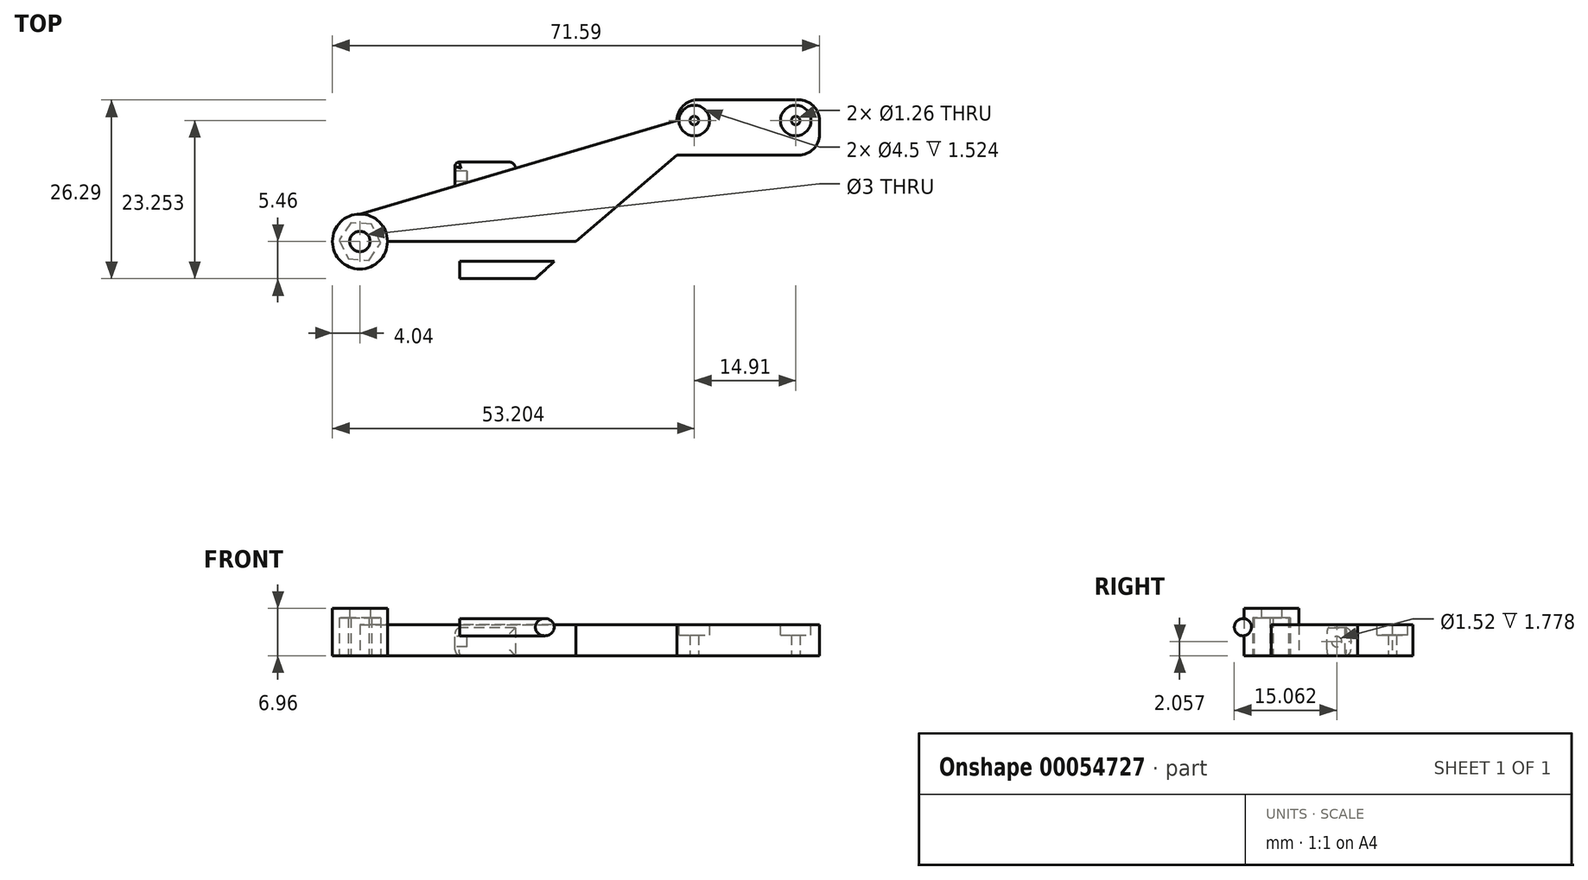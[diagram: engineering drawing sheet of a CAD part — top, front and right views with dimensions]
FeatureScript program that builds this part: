
annotation { "Feature Type Name" : "Feature", "Feature Type Description" : "" }
export const myFeature = defineFeature(function(context is Context, id is Id, definition is map)
    precondition{}
    {
        {
            var Q0;
            Q0=qCreatedBy(makeId("Top.planeOp"),FACE);
            var sketch = newSketch(context, id + "F0", { "sketchPlane" : qUnion([Q0])});
            skLineSegment(sketch, "E0", {"start": v(0, 0) * mm, "end": v(-31.75, 0) * mm});
            skLineSegment(sketch, "E1", {"start": v(-31.75, 0) * mm, "end": v(-46.62, 12.7) * mm});
            skLineSegment(sketch, "E2", {"start": v(-46.62, 12.7) * mm, "end": v(0, 0) * mm});
            skLineSegment(sketch, "E3", {"start": v(0, 0) * mm, "end": v(0, 4.04) * mm});
            skCircle(sketch, "E4", {"center": v(0, 0) * mm, "radius": 4.04 * mm});
            skLineSegment(sketch, "E5.bottom", {"start": v(-46.62, 12.7) * mm, "end": v(-64.5, 12.7) * mm});
            skLineSegment(sketch, "E5.top", {"start": v(-49.67, 20.83) * mm, "end": v(-64.5, 20.83) * mm});
            skLineSegment(sketch, "E5.left", {"start": v(-46.62, 12.7) * mm, "end": v(-46.62, 17.78) * mm});
            skLineSegment(sketch, "E5.right", {"start": v(-67.55, 15.75) * mm, "end": v(-67.55, 17.78) * mm});
            skCircle(sketch, "E6", {"center": v(-49.16, 17.8) * mm, "radius": 0.63 * mm});
            skCircle(sketch, "E7", {"center": v(-64.07, 17.8) * mm, "radius": 0.63 * mm});
            skPoint(sketch, "E8.visualSharp", {"position": v(-67.55, 20.83) * mm});
            skArc(sketch, "E8.filletArc", {"start": v(-64.5, 20.83) * mm, "mid": v(-66.66, 19.94) * mm, "end": v(-67.55, 17.78) * mm});
            skPoint(sketch, "E9.visualSharp", {"position": v(-67.55, 12.7) * mm});
            skArc(sketch, "E9.filletArc", {"start": v(-67.55, 15.75) * mm, "mid": v(-66.66, 13.6) * mm, "end": v(-64.5, 12.7) * mm});
            skPoint(sketch, "E10.visualSharp", {"position": v(-46.62, 20.83) * mm});
            skArc(sketch, "E10.filletArc", {"start": v(-46.62, 17.78) * mm, "mid": v(-47.52, 19.94) * mm, "end": v(-49.67, 20.83) * mm});
            skLineSegment(sketch, "E11", {"start": v(-46.62, 17.78) * mm, "end": v(0, 4.04) * mm});
            skLineSegment(sketch, "E12", {"start": v(-46.62, 12.7) * mm, "end": v(-49.67, 12.7) * mm});
            skLineSegment(sketch, "E13", {"start": v(-46.62, 12.7) * mm, "end": v(-44.3, 10.72) * mm});
            skLineSegment(sketch, "E14", {"start": v(-49.67, 12.7) * mm, "end": v(-44.3, 10.72) * mm});
            skCircle(sketch, "E15", {"center": v(0, 0) * mm, "radius": 1.5 * mm});
            skLineSegment(sketch, "E16", {"start": v(-44.3, 10.72) * mm, "end": v(-20.3, -9.78) * mm});
            skLineSegment(sketch, "E17", {"start": v(-21, -9.17) * mm, "end": v(-44.3, 10.72) * mm});
            skLineSegment(sketch, "E18", {"start": v(-31.75, 0) * mm, "end": v(-22.66, 0) * mm});
            skLineSegment(sketch, "E19", {"start": v(-22.66, 0) * mm, "end": v(-22.66, -4.18) * mm});
            skLineSegment(sketch, "E20", {"start": v(-22.66, 0) * mm, "end": v(-21.74, -2.29) * mm});
            skSolve(sketch);
        }
        {
            var Q0;
            Q0=makeQuery(id+"F0.imprint","IMPRINT",FACE,{"disambiguationData":[TD([[makeQuery(id+"F0.imprint","IMPRINT",EDGE,{"derivedFrom":sQuery(id+"F0.wireOp",EDGE,"E5.bottom")}),-1.0]])]});
            var Q1;
            Q1=makeQuery(id+"F0.imprint","IMPRINT",FACE,{"disambiguationData":[TD([[makeQuery(id+"F0.imprint","IMPRINT",EDGE,{"derivedFrom":sQuery(id+"F0.wireOp",EDGE,"E12")}),1.0]])]});
            var Q2;
            {var subQ0=sQuery(id+"F0.wireOp",EDGE,"E5.left");Q2=makeQuery(id+"F0.imprint","IMPRINT",FACE,{"disambiguationData":[TD([[makeQuery(id+"F0.imprint","IMPRINT",EDGE,{"derivedFrom":subQ0}),-1.0]])]});}
            var Q3;
            {var subQ5=sQuery(id+"F0.wireOp",EDGE,"E1");Q3=makeQuery(id+"F0.imprint","IMPRINT",FACE,{"disambiguationData":[TD([[makeQuery(id+"F0.imprint","IMPRINT",EDGE,{"derivedFrom":subQ5}),-1.0]])]});}
            var Q4;
            {var subQ0=sQuery(id+"F0.wireOp",EDGE,"E4");var subQ1=sQuery(id+"F0.wireOp",EDGE,"E2");var subQ2=makeQuery(id+"F0.imprint","INTERSECT",VERTEX,{"derivedFrom":[subQ1,subQ0]});Q4=makeQuery(id+"F0.imprint","IMPRINT",FACE,{"disambiguationData":[TD([[makeQuery(id+"F0.imprint","IMPRINT",EDGE,{"disambiguationData":[TD([[subQ2,-1.0]])],"derivedFrom":subQ1}),1.0]])]});}
            var Q5;
            {var subQ0=sQuery(id+"F0.wireOp",EDGE,"E4");var subQ1=sQuery(id+"F0.wireOp",EDGE,"E0");var subQ2=makeQuery(id+"F0.imprint","INTERSECT",VERTEX,{"derivedFrom":[subQ1,subQ0]});Q5=makeQuery(id+"F0.imprint","IMPRINT",FACE,{"disambiguationData":[TD([[makeQuery(id+"F0.imprint","IMPRINT",EDGE,{"disambiguationData":[TD([[subQ2,1.0]])],"derivedFrom":subQ1}),-1.0]])]});}
            var Q6;
            {var subQ0=sQuery(id+"F0.wireOp",EDGE,"E4");var subQ1=sQuery(id+"F0.wireOp",EDGE,"E0");var subQ2=makeQuery(id+"F0.imprint","INTERSECT",VERTEX,{"derivedFrom":[subQ1,subQ0]});Q6=makeQuery(id+"F0.imprint","IMPRINT",FACE,{"disambiguationData":[TD([[makeQuery(id+"F0.imprint","IMPRINT",EDGE,{"disambiguationData":[TD([[subQ2,1.0]])],"derivedFrom":subQ1}),1.0]])]});}
            var Q7;
            {var subQ0=sQuery(id+"F0.wireOp",EDGE,"E13");Q7=makeQuery(id+"F0.imprint","IMPRINT",FACE,{"disambiguationData":[TD([[makeQuery(id+"F0.imprint","IMPRINT",EDGE,{"derivedFrom":subQ0}),1.0]])]});}
            extrude(context, id + "F1", {"entities" : qUnion([Q0, Q1, Q2, Q3, Q4, Q5, Q6, Q7]), "depth" : 4.57 * mm});
        }
        {
            var Q0;
            {var subQ0=sQuery(id+"F0.wireOp",EDGE,"E4");var subQ1=sQuery(id+"F0.wireOp",EDGE,"E2");var subQ2=makeQuery(id+"F0.imprint","INTERSECT",VERTEX,{"derivedFrom":[subQ1,subQ0]});Q0=makeQuery(id+"F0.imprint","IMPRINT",FACE,{"disambiguationData":[TD([[makeQuery(id+"F0.imprint","IMPRINT",EDGE,{"disambiguationData":[TD([[subQ2,-1.0]])],"derivedFrom":subQ1}),1.0]])]});}
            var Q1;
            {var subQ0=sQuery(id+"F0.wireOp",EDGE,"E4");var subQ1=sQuery(id+"F0.wireOp",EDGE,"E0");var subQ2=makeQuery(id+"F0.imprint","INTERSECT",VERTEX,{"derivedFrom":[subQ1,subQ0]});Q1=makeQuery(id+"F0.imprint","IMPRINT",FACE,{"disambiguationData":[TD([[makeQuery(id+"F0.imprint","IMPRINT",EDGE,{"disambiguationData":[TD([[subQ2,1.0]])],"derivedFrom":subQ1}),1.0]])]});}
            var Q2;
            {var subQ0=sQuery(id+"F0.wireOp",EDGE,"E4");var subQ1=sQuery(id+"F0.wireOp",EDGE,"E0");var subQ2=makeQuery(id+"F0.imprint","INTERSECT",VERTEX,{"derivedFrom":[subQ1,subQ0]});Q2=makeQuery(id+"F0.imprint","IMPRINT",FACE,{"disambiguationData":[TD([[makeQuery(id+"F0.imprint","IMPRINT",EDGE,{"disambiguationData":[TD([[subQ2,1.0]])],"derivedFrom":subQ1}),-1.0]])]});}
            extrude(context, id + "F2", {"entities" : qUnion([Q0, Q1, Q2]), "operationType" : NewBodyOperationType.ADD, "depth" : 6.96 * mm});
        }
        {
            var Q0;
            Q0=makeQuery(id+"F1.opExtrude","CAP_FACE",FACE,{"disambiguationData":[OSD([sQuery(id+"F0.wireOp",EDGE,"E0"),sQuery(id+"F0.wireOp",EDGE,"E1"),sQuery(id+"F0.wireOp",EDGE,"E4"),sQuery(id+"F0.wireOp",EDGE,"E5.bottom"),sQuery(id+"F0.wireOp",EDGE,"E5.top"),sQuery(id+"F0.wireOp",EDGE,"E5.right"),sQuery(id+"F0.wireOp",EDGE,"E6"),sQuery(id+"F0.wireOp",EDGE,"E7"),sQuery(id+"F0.wireOp",EDGE,"E8.filletArc"),sQuery(id+"F0.wireOp",EDGE,"E9.filletArc"),sQuery(id+"F0.wireOp",EDGE,"E10.filletArc"),sQuery(id+"F0.wireOp",EDGE,"E11"),sQuery(id+"F0.wireOp",EDGE,"E14"),sQuery(id+"F0.wireOp",EDGE,"E15")])],"isStart":false});
            var sketch = newSketch(context, id + "F3", { "sketchPlane" : qUnion([Q0])});
            skCircle(sketch, "E21", {"center": v(-64.07, 17.8) * mm, "radius": 2.25 * mm});
            skCircle(sketch, "E22", {"center": v(-49.16, 17.8) * mm, "radius": 1.35 * mm});
            skCircle(sketch, "E23", {"center": v(-49.16, 17.8) * mm, "radius": 2.25 * mm});
            skSolve(sketch);
        }
        {
            var Q0;
            Q0=makeQuery(id+"F3.imprint","IMPRINT",FACE,{"disambiguationData":[TD([[makeQuery(id+"F3.imprint","IMPRINT",EDGE,{"derivedFrom":sQuery(id+"F3.wireOp",EDGE,"E21")}),1.0]])]});
            var Q1;
            Q1=makeQuery(id+"F3.imprint","IMPRINT",FACE,{"disambiguationData":[TD([[makeQuery(id+"F3.imprint","IMPRINT",EDGE,{"derivedFrom":sQuery(id+"F3.wireOp",EDGE,"E22")}),-1.0]])]});
            var Q2;
            Q2=makeQuery(id+"F3.imprint","IMPRINT",FACE,{"disambiguationData":[TD([[makeQuery(id+"F3.imprint","IMPRINT",EDGE,{"derivedFrom":sQuery(id+"F3.wireOp",EDGE,"E22")}),1.0]])]});
            extrude(context, id + "F4", {"entities" : qUnion([Q0, Q1, Q2]), "operationType" : NewBodyOperationType.REMOVE, "oppositeDirection" : true, "depth" : 1.52 * mm});
        }
        {
            var Q0;
            Q0=qCreatedBy(makeId("Top.planeOp"),FACE);
            var sketch = newSketch(context, id + "F5", { "sketchPlane" : qUnion([Q0])});
            skLineSegment(sketch, "E24", {"start": v(0, 0) * mm, "end": v(-14.7, 0) * mm});
            skLineSegment(sketch, "E25", {"start": v(-14.7, 0) * mm, "end": v(-14.7, -8.38) * mm});
            skLineSegment(sketch, "E26", {"start": v(-14.7, 0) * mm, "end": v(-31.75, 0) * mm});
            skLineSegment(sketch, "E27", {"start": v(-14.7, -8.38) * mm, "end": v(-22.62, -8.38) * mm});
            skLineSegment(sketch, "E28", {"start": v(-22.62, -8.38) * mm, "end": v(-31.75, 0) * mm});
            skLineSegment(sketch, "E29", {"start": v(-14.6, 11.68) * mm, "end": v(-22.86, 11.68) * mm});
            skLineSegment(sketch, "E30", {"start": v(-22.86, 11.68) * mm, "end": v(-22.86, 4.7) * mm});
            skLineSegment(sketch, "E31", {"start": v(-22.86, 4.7) * mm, "end": v(-13.97, 4.7) * mm});
            skLineSegment(sketch, "E32", {"start": v(-13.97, 4.7) * mm, "end": v(-13.97, 11.05) * mm});
            skPoint(sketch, "E33.visualSharp", {"position": v(-13.97, 11.68) * mm});
            skArc(sketch, "E33.filletArc", {"start": v(-13.97, 11.05) * mm, "mid": v(-14.16, 11.5) * mm, "end": v(-14.6, 11.68) * mm});
            skSolve(sketch);
        }
        {
            var Q0;
            Q0=makeQuery(id+"F5.imprint","IMPRINT",FACE,{"disambiguationData":[TD([[makeQuery(id+"F5.imprint","IMPRINT",EDGE,{"derivedFrom":sQuery(id+"F5.wireOp",EDGE,"E29")}),1.0]])]});
            extrude(context, id + "F6", {"entities" : qUnion([Q0]), "operationType" : NewBodyOperationType.ADD, "depth" : 4.11 * mm});
        }
        {
            var Q0;
            Q0=makeQuery(id+"F5.imprint","IMPRINT",FACE,{"disambiguationData":[TD([[makeQuery(id+"F5.imprint","IMPRINT",EDGE,{"derivedFrom":sQuery(id+"F5.wireOp",EDGE,"E25")}),-1.0]])]});
            extrude(context, id + "F7", {"entities" : qUnion([Q0]), "operationType" : NewBodyOperationType.ADD, "depth" : 8.38 * mm});
        }
        {
            var Q0;
            Q0=makeQuery(id+"F7.opExtrude","CAP_EDGE",EDGE,{"disambiguationData":[OSD([sQuery(id+"F5.wireOp",EDGE,"E26")])],"isStart":false});
            var Q1;
            Q1=makeQuery(id+"F7.opExtrude","CAP_EDGE",EDGE,{"disambiguationData":[OSD([sQuery(id+"F5.wireOp",EDGE,"E27")])],"isStart":false});
            var Q2;
            Q2=makeQuery(id+"F7.opExtrude","CAP_EDGE",EDGE,{"disambiguationData":[OSD([sQuery(id+"F5.wireOp",EDGE,"E27")])],"isStart":true});
            fillet(context, id + "F8", {"entities" : qUnion([Q0, Q1, Q2]), "radius" : 3.8 * mm, "tangentPropagation" : true, "allowEdgeOverflow" : false});
        }
        {
            var Q0;
            Q0=makeQuery(id+"F7.opExtrude","SWEPT_FACE",FACE,{"disambiguationData":[OSD([sQuery(id+"F5.wireOp",EDGE,"E25")])]});
            var sketch = newSketch(context, id + "F9", { "sketchPlane" : qUnion([Q0])});
            skLineSegment(sketch, "E34", {"start": v(-4.2, 8.38) * mm, "end": v(-4.2, 0) * mm});
            skCircle(sketch, "E35", {"center": v(-4.2, 4.2) * mm, "radius": 1.27 * mm});
            skSolve(sketch);
        }
        {
            var Q0;
            {var subQ0=sQuery(id+"F9.wireOp",EDGE,"E35");var subQ1=sQuery(id+"F9.wireOp",EDGE,"E34");var subQ2=makeQuery(id+"F9.imprint","INTERSECT",VERTEX,{"disambiguationData":[OD(0.0)],"derivedFrom":[subQ1,subQ0]});Q0=makeQuery(id+"F9.imprint","IMPRINT",FACE,{"disambiguationData":[TD([[makeQuery(id+"F9.imprint","IMPRINT",EDGE,{"disambiguationData":[TD([[subQ2,-1.0]])],"derivedFrom":subQ1}),-1.0]])]});}
            var Q1;
            {var subQ0=sQuery(id+"F9.wireOp",EDGE,"E35");var subQ1=sQuery(id+"F9.wireOp",EDGE,"E34");var subQ2=makeQuery(id+"F9.imprint","INTERSECT",VERTEX,{"disambiguationData":[OD(0.0)],"derivedFrom":[subQ1,subQ0]});Q1=makeQuery(id+"F9.imprint","IMPRINT",FACE,{"disambiguationData":[TD([[makeQuery(id+"F9.imprint","IMPRINT",EDGE,{"disambiguationData":[TD([[subQ2,-1.0]])],"derivedFrom":subQ1}),1.0]])]});}
            var Q2;
            Q2=qSketchRegion(id+"F12",true);
            extrude(context, id + "F10", {"entities" : qUnion([Q0, Q1, Q2]), "operationType" : NewBodyOperationType.REMOVE, "oppositeDirection" : true, "depth" : 25.4 * mm});
        }
        {
            var Q0;
            Q0=makeQuery(id+"F7.opExtrude","SWEPT_FACE",FACE,{"disambiguationData":[OSD([sQuery(id+"F5.wireOp",EDGE,"E25")])]});
            cPlane(context, id + "F11", {"entities" : qUnion([Q0]), "cplaneType" : CPlaneType.OFFSET, "offset" : 2.3 * mm, "oppositeDirection" : true, "width" : 152.4 * mm, "height" : 152.4 * mm});
        }
        {
            var Q0;
            Q0=qCreatedBy(id+"F11.planeOp",FACE);
            var sketch = newSketch(context, id + "F12", { "sketchPlane" : qUnion([Q0])});
            skCircle(sketch, "E36", {"center": v(-4.19, 4.19) * mm, "radius": 2.8 * mm});
            skCircle(sketch, "E37", {"center": v(-4.19, 4.19) * mm, "radius": 1.27 * mm});
            skSolve(sketch);
        }
        {
            var Q0;
            Q0=qSketchRegion(id+"F12",true);
            extrude(context, id + "F13", {"entities" : qUnion([Q0]), "operationType" : NewBodyOperationType.REMOVE, "oppositeDirection" : true, "depth" : 25.4 * mm});
        }
        {
            var Q0;
            Q0=makeQuery(id+"F6.opExtrude","SWEPT_EDGE",EDGE,{"disambiguationData":[OSD([sQuery(id+"F5.wireOp",EDGE,"E29"),sQuery(id+"F5.wireOp",EDGE,"E30")])]});
            var Q1;
            Q1=makeQuery(id+"F6.opExtrude","CAP_EDGE",EDGE,{"disambiguationData":[OSD([sQuery(id+"F5.wireOp",EDGE,"E29")])],"isStart":false});
            var Q2;
            Q2=makeQuery(id+"F6.opExtrude","CAP_EDGE",EDGE,{"disambiguationData":[OSD([sQuery(id+"F5.wireOp",EDGE,"E29")])],"isStart":true});
            var Q3;
            Q3=makeQuery(id+"F6.opExtrude","SWEPT_EDGE",EDGE,{"disambiguationData":[OSD([sQuery(id+"F5.wireOp",EDGE,"E29"),sQuery(id+"F5.wireOp",EDGE,"E33.filletArc")])]});
            var Q4;
            Q4=makeQuery(id+"F6.opExtrude","SWEPT_EDGE",EDGE,{"disambiguationData":[OSD([sQuery(id+"F5.wireOp",EDGE,"E32"),sQuery(id+"F5.wireOp",EDGE,"E33.filletArc")])]});
            fillet(context, id + "F14", {"entities" : qUnion([Q0, Q1, Q2, Q3, Q4]), "radius" : 0.89 * mm, "tangentPropagation" : true, "allowEdgeOverflow" : false});
        }
        {
            var Q0;
            Q0=makeQuery(id+"F6.opExtrude","SWEPT_FACE",FACE,{"disambiguationData":[OSD([sQuery(id+"F5.wireOp",EDGE,"E32")])]});
            var sketch = newSketch(context, id + "F15", { "sketchPlane" : qUnion([Q0])});
            skPoint(sketch, "E38.endSnap0", {"position": v(9.6, 3.23) * mm});
            skCircle(sketch, "E39", {"center": v(9.6, 2.06) * mm, "radius": 0.76 * mm});
            skSolve(sketch);
        }
        {
            var Q0;
            Q0=qSketchRegion(id+"F15",true);
            extrude(context, id + "F16", {"entities" : qUnion([Q0]), "operationType" : NewBodyOperationType.REMOVE, "oppositeDirection" : true, "depth" : 1.78 * mm});
        }
        {
            var Q0;
            {var subQ0=sQuery(id+"F0.wireOp",EDGE,"E4");var subQ1=sQuery(id+"F0.wireOp",EDGE,"E0");var subQ2=makeQuery(id+"F0.imprint","INTERSECT",VERTEX,{"derivedFrom":[subQ1,subQ0]});Q0=makeQuery(id+"F0.imprint","IMPRINT",FACE,{"disambiguationData":[TD([[makeQuery(id+"F0.imprint","IMPRINT",EDGE,{"disambiguationData":[TD([[subQ2,1.0]])],"derivedFrom":subQ1}),1.0]])]});}
            var sketch = newSketch(context, id + "F17", { "sketchPlane" : qUnion([Q0])});
            skCircle(sketch, "E40", {"center": v(0, 0) * mm, "radius": 1.5 * mm});
            skLineSegment(sketch, "E41.1", {"start": v(1.72, -2.55) * mm, "end": v(-1.35, -2.76) * mm});
            skLineSegment(sketch, "E41.2", {"start": v(-1.35, -2.76) * mm, "end": v(-3.07, -0.21) * mm});
            skLineSegment(sketch, "E41.3", {"start": v(-3.07, -0.21) * mm, "end": v(-1.72, 2.55) * mm});
            skLineSegment(sketch, "E41.4", {"start": v(-1.72, 2.55) * mm, "end": v(1.35, 2.76) * mm});
            skLineSegment(sketch, "E41.5", {"start": v(1.35, 2.76) * mm, "end": v(3.07, 0.21) * mm});
            skLineSegment(sketch, "E42", {"start": v(3.07, 0.21) * mm, "end": v(1.72, -2.55) * mm});
            skLineSegment(sketch, "E43", {"start": v(0, 0) * mm, "end": v(1.35, 2.76) * mm});
            skLineSegment(sketch, "E44", {"start": v(0, 0) * mm, "end": v(-1.35, -2.76) * mm});
            skSolve(sketch);
        }
        {
            var Q0;
            Q0=qSketchRegion(id+"F17",true);
            extrude(context, id + "F18", {"entities" : qUnion([Q0]), "operationType" : NewBodyOperationType.REMOVE, "depth" : 5.6 * mm});
        }
        {
            var Q0;
            Q0=qCreatedBy(makeId("Right.planeOp"),FACE);
            cPlane(context, id + "F19", {"entities" : qUnion([Q0]), "cplaneType" : CPlaneType.OFFSET, "offset" : 12.7 * mm, "width" : 152.4 * mm, "height" : 152.4 * mm});
        }
        {
            var Q0;
            Q0=makeQuery(id+"F1.opExtrude","SWEPT_BODY",BODY,{"disambiguationData":[OSD([sQuery(id+"F0.wireOp",EDGE,"E0"),sQuery(id+"F0.wireOp",EDGE,"E4"),sQuery(id+"F0.wireOp",EDGE,"E5.bottom"),sQuery(id+"F0.wireOp",EDGE,"E5.top"),sQuery(id+"F0.wireOp",EDGE,"E5.right"),sQuery(id+"F0.wireOp",EDGE,"E6"),sQuery(id+"F0.wireOp",EDGE,"E7"),sQuery(id+"F0.wireOp",EDGE,"E8.filletArc"),sQuery(id+"F0.wireOp",EDGE,"E9.filletArc"),sQuery(id+"F0.wireOp",EDGE,"E10.filletArc"),sQuery(id+"F0.wireOp",EDGE,"E11"),sQuery(id+"F0.wireOp",EDGE,"E14"),sQuery(id+"F0.wireOp",EDGE,"E15"),sQuery(id+"F0.wireOp",EDGE,"E17"),sQuery(id+"F0.wireOp",EDGE,"E18")])]});
            var Q1;
            Q1=qCreatedBy(id+"F19.planeOp",FACE);
            mirror(context, id + "F20", {"entities" : qUnion([Q0]), "mirrorPlane" : qUnion([Q1])});
        }
        {
            var Q0;
            Q0=makeQuery(id+"F1.opExtrude","SWEPT_BODY",BODY,{"disambiguationData":[OSD([sQuery(id+"F0.wireOp",EDGE,"E0"),sQuery(id+"F0.wireOp",EDGE,"E4"),sQuery(id+"F0.wireOp",EDGE,"E5.bottom"),sQuery(id+"F0.wireOp",EDGE,"E5.top"),sQuery(id+"F0.wireOp",EDGE,"E5.right"),sQuery(id+"F0.wireOp",EDGE,"E6"),sQuery(id+"F0.wireOp",EDGE,"E7"),sQuery(id+"F0.wireOp",EDGE,"E8.filletArc"),sQuery(id+"F0.wireOp",EDGE,"E9.filletArc"),sQuery(id+"F0.wireOp",EDGE,"E10.filletArc"),sQuery(id+"F0.wireOp",EDGE,"E11"),sQuery(id+"F0.wireOp",EDGE,"E14"),sQuery(id+"F0.wireOp",EDGE,"E15"),sQuery(id+"F0.wireOp",EDGE,"E17"),sQuery(id+"F0.wireOp",EDGE,"E18")])]});
            deleteBodies(context, id + "F21", {"entities" : qUnion([Q0])});
        }
    });
